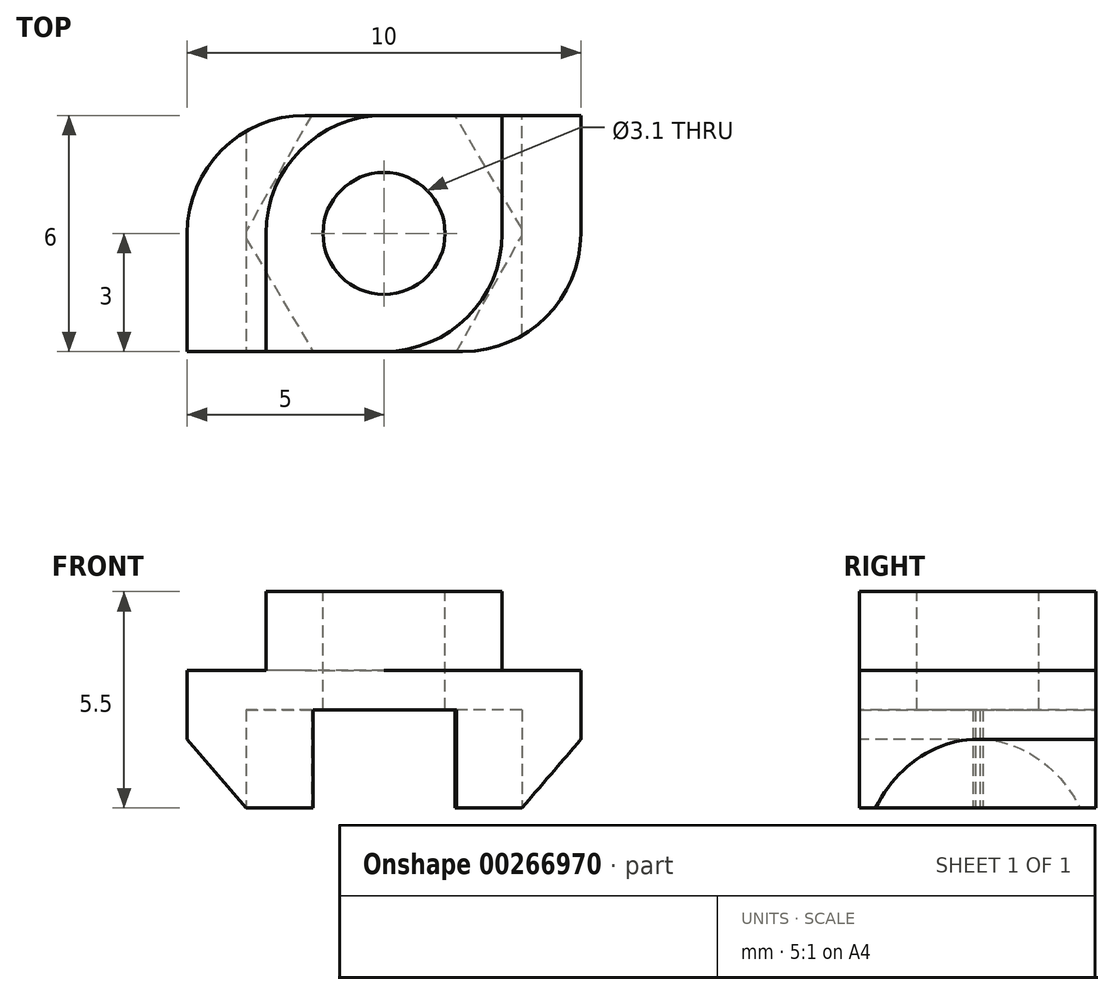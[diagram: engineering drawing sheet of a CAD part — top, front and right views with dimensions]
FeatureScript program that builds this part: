
annotation { "Feature Type Name" : "Feature", "Feature Type Description" : "" }
export const myFeature = defineFeature(function(context is Context, id is Id, definition is map)
    precondition{}
    {
        {
            var Q0;
            Q0=qCreatedBy(makeId("Top.planeOp"),FACE);
            var sketch = newSketch(context, id + "F0", { "sketchPlane" : qUnion([Q0])});
            skLineSegment(sketch, "E0.bottom", {"start": v(-5, -3) * mm, "end": v(2, -3) * mm});
            skLineSegment(sketch, "E0.top", {"start": v(-2, 3) * mm, "end": v(5, 3) * mm});
            skLineSegment(sketch, "E0.left", {"start": v(-5, -3) * mm, "end": v(-5, 0) * mm});
            skLineSegment(sketch, "E0.right", {"start": v(5, 0) * mm, "end": v(5, 3) * mm});
            skPoint(sketch, "E0.middle", {"position": v(0, 0) * mm});
            skArc(sketch, "E1", {"start": v(-2, 3) * mm, "mid": v(-4.12, 2.12) * mm, "end": v(-5, 0) * mm});
            skArc(sketch, "E2", {"start": v(2, -3) * mm, "mid": v(4.12, -2.12) * mm, "end": v(5, 0) * mm});
            skPoint(sketch, "E3.orphan", {"position": v(-5, 3) * mm});
            skPoint(sketch, "E4.orphan", {"position": v(5, -3) * mm});
            skSolve(sketch);
        }
        {
            var Q0;
            Q0 = qSketchRegion(id + "F0", true);
            extrude(context, id + "F1", {"entities" : qUnion([Q0]), "depth" : 3.5 * mm});
        }
        {
            var Q0;
            Q0=makeQuery(id+"F1.opExtrude","CAP_FACE",FACE,{"disambiguationData":[OSD([sQuery(id+"F0.wireOp",EDGE,"E0.bottom"),sQuery(id+"F0.wireOp",EDGE,"E0.top"),sQuery(id+"F0.wireOp",EDGE,"E0.left"),sQuery(id+"F0.wireOp",EDGE,"E0.right"),sQuery(id+"F0.wireOp",EDGE,"E1"),sQuery(id+"F0.wireOp",EDGE,"E2")])],"isStart":false});
            var sketch = newSketch(context, id + "F2", { "sketchPlane" : qUnion([Q0])});
            skLineSegment(sketch, "E5.bottom", {"start": v(3, 3) * mm, "end": v(0, 3) * mm});
            skLineSegment(sketch, "E5.top", {"start": v(0, -3) * mm, "end": v(-3, -3) * mm});
            skLineSegment(sketch, "E5.left", {"start": v(3, 3) * mm, "end": v(3, 0) * mm});
            skLineSegment(sketch, "E5.right", {"start": v(-3, 0) * mm, "end": v(-3, -3) * mm});
            skPoint(sketch, "E5.middle", {"position": v(0, 0) * mm});
            skArc(sketch, "E6", {"start": v(0, -3) * mm, "mid": v(2.12, -2.12) * mm, "end": v(3, 0) * mm});
            skPoint(sketch, "E7.orphan", {"position": v(-3, 3) * mm});
            skPoint(sketch, "E8.orphan", {"position": v(3, -3) * mm});
            skArc(sketch, "E9.trimOffspring", {"start": v(0, 3) * mm, "mid": v(-2.12, 2.12) * mm, "end": v(-3, 0) * mm});
            skSolve(sketch);
        }
        {
            var Q0;
            Q0=makeQuery(id+"F2.imprint","IMPRINT",FACE,{"disambiguationData":[TD([[makeQuery(id+"F2.imprint","IMPRINT",EDGE,{"derivedFrom":sQuery(id+"F2.wireOp",EDGE,"E5.bottom")}),-1.0]])]});
            extrude(context, id + "F3", {"entities" : qUnion([Q0]), "operationType" : NewBodyOperationType.ADD, "depth" : 2 * mm});
        }
        {
            var Q0;
            Q0=makeQuery(id+"F3.opExtrude","CAP_FACE",FACE,{"disambiguationData":[OSD([sQuery(id+"F2.wireOp",EDGE,"E5.bottom"),sQuery(id+"F2.wireOp",EDGE,"E5.top"),sQuery(id+"F2.wireOp",EDGE,"E5.left"),sQuery(id+"F2.wireOp",EDGE,"E5.right"),sQuery(id+"F2.wireOp",EDGE,"E6"),sQuery(id+"F2.wireOp",EDGE,"E9.trimOffspring")])],"isStart":false});
            var sketch = newSketch(context, id + "F4", { "sketchPlane" : qUnion([Q0])});
            skCircle(sketch, "E10", {"center": v(0, 0) * mm, "radius": 1.55 * mm});
            skSolve(sketch);
        }
        {
            var Q0;
            Q0 = qSketchRegion(id + "F4", true);
            extrude(context, id + "F5", {"entities" : qUnion([Q0]), "operationType" : NewBodyOperationType.REMOVE, "oppositeDirection" : true, "depth" : 25 * mm});
        }
        {
            var Q0;
            Q0=makeQuery(id+"F3.boolean.opBoolean","MERGE",FACE,{"derivedFrom":[makeQuery(id+"F1.opExtrude","SWEPT_FACE",FACE,{"disambiguationData":[OSD([sQuery(id+"F0.wireOp",EDGE,"E0.bottom")])]}),makeQuery(id+"F3.opExtrude","SWEPT_FACE",FACE,{"disambiguationData":[OSD([sQuery(id+"F2.wireOp",EDGE,"E5.top")])]})]});
            var sketch = newSketch(context, id + "F6", { "sketchPlane" : qUnion([Q0])});
            skLineSegment(sketch, "E11", {"start": v(-5, 1.75) * mm, "end": v(-3.5, 0) * mm});
            skLineSegment(sketch, "E12", {"start": v(-3.5, 0) * mm, "end": v(-5, 0) * mm});
            skLineSegment(sketch, "E13", {"start": v(-5, 0) * mm, "end": v(-5, 1.75) * mm});
            skSolve(sketch);
        }
        {
            var Q0;
            Q0=makeQuery(id+"F6.imprint","IMPRINT",FACE,{"disambiguationData":[TD([[makeQuery(id+"F6.imprint","IMPRINT",EDGE,{"derivedFrom":sQuery(id+"F6.wireOp",EDGE,"E11")}),-1.0]])]});
            extrude(context, id + "F7", {"entities" : qUnion([Q0]), "operationType" : NewBodyOperationType.REMOVE, "oppositeDirection" : true, "depth" : 25 * mm});
        }
        {
            var Q0;
            Q0=makeQuery(id+"F3.boolean.opBoolean","MERGE",FACE,{"derivedFrom":[makeQuery(id+"F1.opExtrude","SWEPT_FACE",FACE,{"disambiguationData":[OSD([sQuery(id+"F0.wireOp",EDGE,"E0.top")])]}),makeQuery(id+"F3.opExtrude","SWEPT_FACE",FACE,{"disambiguationData":[OSD([sQuery(id+"F2.wireOp",EDGE,"E5.bottom")])]})]});
            var sketch = newSketch(context, id + "F8", { "sketchPlane" : qUnion([Q0])});
            skLineSegment(sketch, "E14", {"start": v(-3.5, 0) * mm, "end": v(-5, 0) * mm});
            skLineSegment(sketch, "E15", {"start": v(-5, 0) * mm, "end": v(-5, 1.75) * mm});
            skLineSegment(sketch, "E16", {"start": v(-5, 1.75) * mm, "end": v(-3.5, 0) * mm});
            skSolve(sketch);
        }
        {
            var Q0;
            Q0=makeQuery(id+"F8.imprint","IMPRINT",FACE,{"disambiguationData":[TD([[makeQuery(id+"F8.imprint","IMPRINT",EDGE,{"derivedFrom":sQuery(id+"F8.wireOp",EDGE,"E14")}),-1.0]])]});
            extrude(context, id + "F9", {"entities" : qUnion([Q0]), "operationType" : NewBodyOperationType.REMOVE, "oppositeDirection" : true, "depth" : 25 * mm});
        }
        {
            var Q0;
            Q0=makeQuery(id+"F1.opExtrude","CAP_FACE",FACE,{"disambiguationData":[OSD([sQuery(id+"F0.wireOp",EDGE,"E0.bottom"),sQuery(id+"F0.wireOp",EDGE,"E0.top"),sQuery(id+"F0.wireOp",EDGE,"E0.left"),sQuery(id+"F0.wireOp",EDGE,"E0.right"),sQuery(id+"F0.wireOp",EDGE,"E1"),sQuery(id+"F0.wireOp",EDGE,"E2")])],"isStart":true});
            var sketch = newSketch(context, id + "F10", { "sketchPlane" : qUnion([Q0])});
            skCircle(sketch, "E17.cCircle", {"center": v(0, 0) * mm, "radius": 3.08 * mm, "construction": true});
            skLineSegment(sketch, "E17.0", {"start": v(3.55, -0.04) * mm, "end": v(1.75, -3.1) * mm});
            skLineSegment(sketch, "E17.1", {"start": v(1.75, -3.1) * mm, "end": v(-1.8, -3.06) * mm});
            skLineSegment(sketch, "E17.2", {"start": v(-1.8, -3.06) * mm, "end": v(-3.55, 0.04) * mm});
            skLineSegment(sketch, "E17.3", {"start": v(-3.55, 0.04) * mm, "end": v(-1.75, 3.1) * mm});
            skLineSegment(sketch, "E17.4", {"start": v(-1.75, 3.1) * mm, "end": v(1.8, 3.06) * mm});
            skLineSegment(sketch, "E17.5", {"start": v(1.8, 3.06) * mm, "end": v(3.55, -0.04) * mm});
            skPoint(sketch, "E17.0.midPoint", {"position": v(2.65, -1.57) * mm});
            skSolve(sketch);
        }
        {
            var Q0;
            {var subQ1=sQuery(id+"F0.wireOp",EDGE,"E0.bottom");var subQ2=makeQuery(id+"F1.opExtrude","CAP_EDGE",EDGE,{"disambiguationData":[OSD([subQ1])],"isStart":true});var subQ10=sQuery(id+"F10.wireOp",EDGE,"E17.3");var subQ14=makeQuery(id+"F10.imprint","INTERSECT",VERTEX,{"derivedFrom":[subQ2,subQ10]});Q0=makeQuery(id+"F10.imprint","IMPRINT",FACE,{"disambiguationData":[TD([[makeQuery(id+"F10.imprint","IMPRINT",EDGE,{"disambiguationData":[TD([[subQ14,-1.0]])],"derivedFrom":subQ2}),-1.0]])]});}
            extrude(context, id + "F11", {"entities" : qUnion([Q0]), "operationType" : NewBodyOperationType.REMOVE, "oppositeDirection" : true, "depth" : 2.5 * mm});
        }
    });
